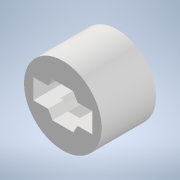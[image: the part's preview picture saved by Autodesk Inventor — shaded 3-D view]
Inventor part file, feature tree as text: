
AUTODESK INVENTOR PART (.ipt)
format: ipt  version: 2022 (Build 260153000, 153)  size: 171,008 bytes
history: native  units: mm
features: extrude x3, sketch x3, other x3, plane x1, reference x1, projected_geometry x1
ambient origin geometry x8: Origin, YZ Plane, XZ Plane, XY Plane, X Axis, Y Axis, Z Axis, Center Point
bodies: Solid1 (feature_tree)
feature tree (12):
  extrude  "Extrusion1"  Depth=10.0mm
  sketch  "Sketch2"  dims[d2=2.0mm d3=5.0mm d4=0.0mm d5=0.0mm d6=40.0mm d8=360.0deg]
  plane  "Work Plane1"
  extrude  "Extrusion2"  Depth=5.0mm TaperAngle=360.0deg
  extrude  "Extrusion3"  TaperAngle=0.0deg  [1 undecoded]
  sketch  "Sketch1"  dims[d0=10.0mm d1=0.3mm]
  reference  "Reference1"
  projected_geometry  "Projected Loop1"
  sketch  "Sketch3"  dims[d10=2.0mm d11=0.0mm d12=0.0mm d13=0.0mm]
  other  "<userpath>\OneDrive - Imperial College London\ROBOICP\new vial holder assembly.iam"
  other  "new vial holder assembly.iam"
  other  "Mixer:1"
note: 1 required parameter value undecoded (feature->parameter linkage not recoverable at this tier; creation-order binding heuristic only, values carry confidence <= 0.55)
